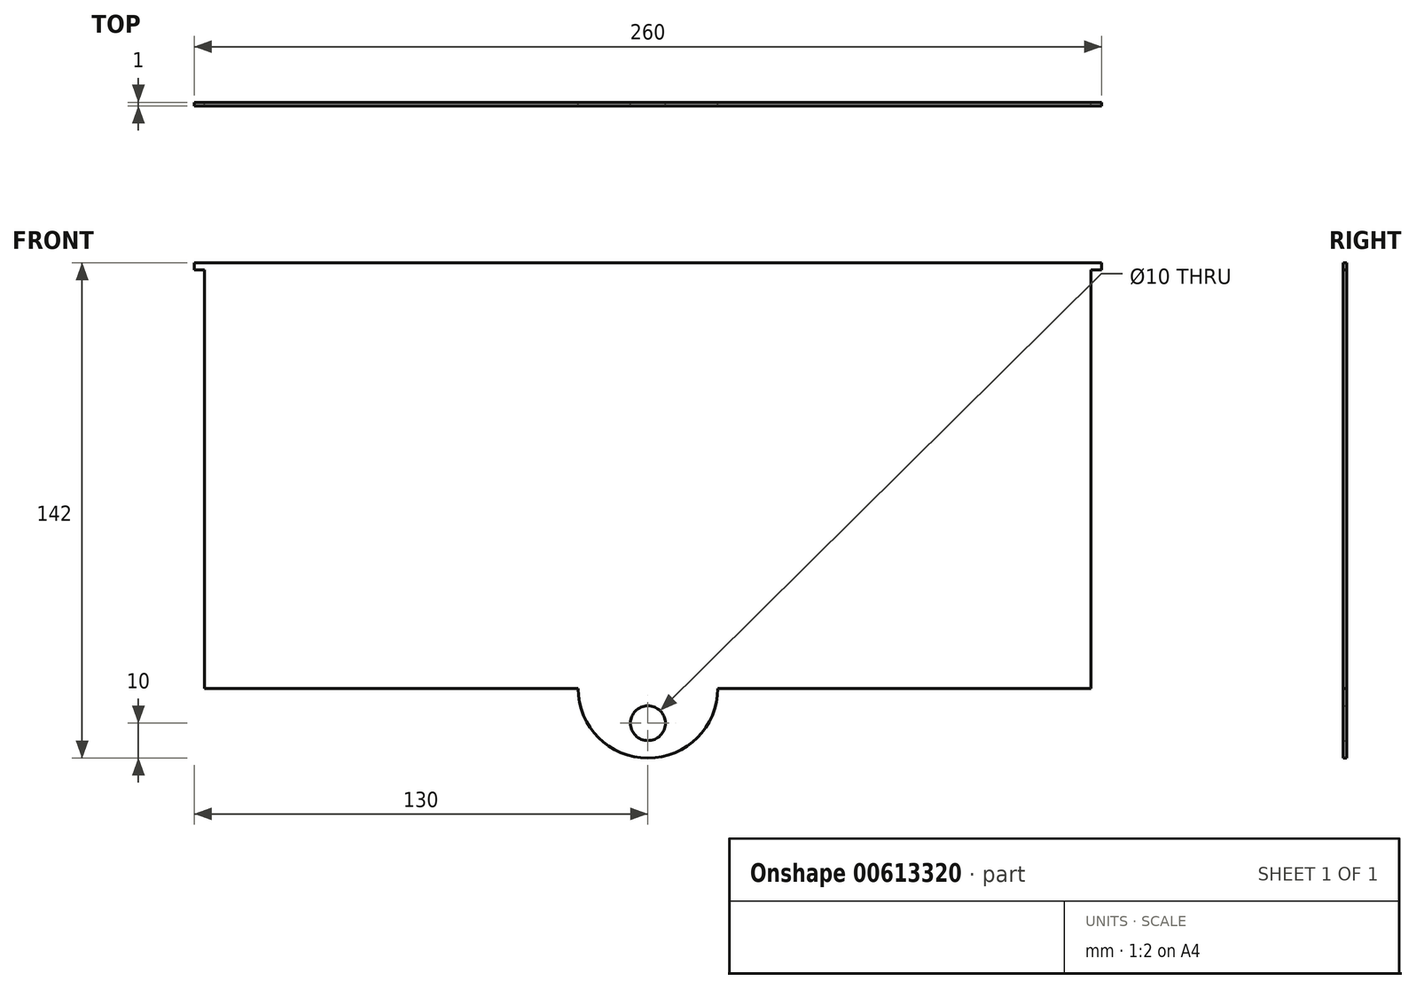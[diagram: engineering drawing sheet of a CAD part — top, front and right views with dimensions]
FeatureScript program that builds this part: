
annotation { "Feature Type Name" : "Feature", "Feature Type Description" : "" }
export const myFeature = defineFeature(function(context is Context, id is Id, definition is map)
    precondition{}
    {
        {
            var Q0;
            Q0=qCreatedBy(makeId("Front.planeOp"),FACE);
            var sketch = newSketch(context, id + "F0", { "sketchPlane" : qUnion([Q0])});
            skLineSegment(sketch, "E0", {"start": v(-127, 120) * mm, "end": v(-127, 0) * mm});
            skLineSegment(sketch, "E1", {"start": v(-127, 0) * mm, "end": v(-20, 0) * mm});
            skLineSegment(sketch, "E2", {"start": v(127, 0) * mm, "end": v(127, 120) * mm});
            skLineSegment(sketch, "E3", {"start": v(127, 120) * mm, "end": v(130, 120) * mm});
            skLineSegment(sketch, "E4", {"start": v(130, 120) * mm, "end": v(130, 122) * mm});
            skLineSegment(sketch, "E5", {"start": v(130, 122) * mm, "end": v(-130, 122) * mm});
            skLineSegment(sketch, "E6", {"start": v(-130, 122) * mm, "end": v(-130, 120) * mm});
            skLineSegment(sketch, "E7", {"start": v(-130, 120) * mm, "end": v(-127, 120) * mm});
            skArc(sketch, "E8", {"start": v(-20, 0) * mm, "mid": v(0, -20) * mm, "end": v(20, 0) * mm});
            skCircle(sketch, "E9", {"center": v(0, -10) * mm, "radius": 5 * mm});
            skLineSegment(sketch, "E10.trimOffspring", {"start": v(20, 0) * mm, "end": v(127, 0) * mm});
            skSolve(sketch);
        }
        {
            var Q0;
            Q0 = qSketchRegion(id + "F0", true);
            extrude(context, id + "F1", {"entities" : qUnion([Q0]), "depth" : 1 * mm, "offsetDistance" : 25 * mm});
        }
    });
